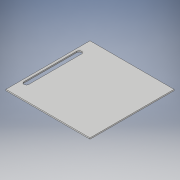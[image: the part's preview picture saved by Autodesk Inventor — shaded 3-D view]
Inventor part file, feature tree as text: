
AUTODESK INVENTOR PART (.ipt)
format: ipt  version: 2019 (Build 230136000, 136)  size: 110,080 bytes
history: native  units: in
note: dims shown in document units (in); Inventor stores cm internally (conversion verified against a paired STEP export)
features: extrude x2, sketch x2
ambient origin geometry x8: Origin, YZ Plane, XZ Plane, XY Plane, X Axis, Y Axis, Z Axis, Center Point
bodies: Solid1 (feature_tree)
feature tree (4):
  extrude  "Extrusion1"  Depth=17.5in
  extrude  "Extrusion3"  Depth=17.5in
  sketch  "Sketch1"  dims[d0=17.5in d1=17.5in]
  sketch  "Sketch2"  dims[d2=0.25in d3=0.0in d8=17.5in d12=1.0in d13=0.5in d14=12.0in d15=2.75in d16=1.0in d17=0.0in]
